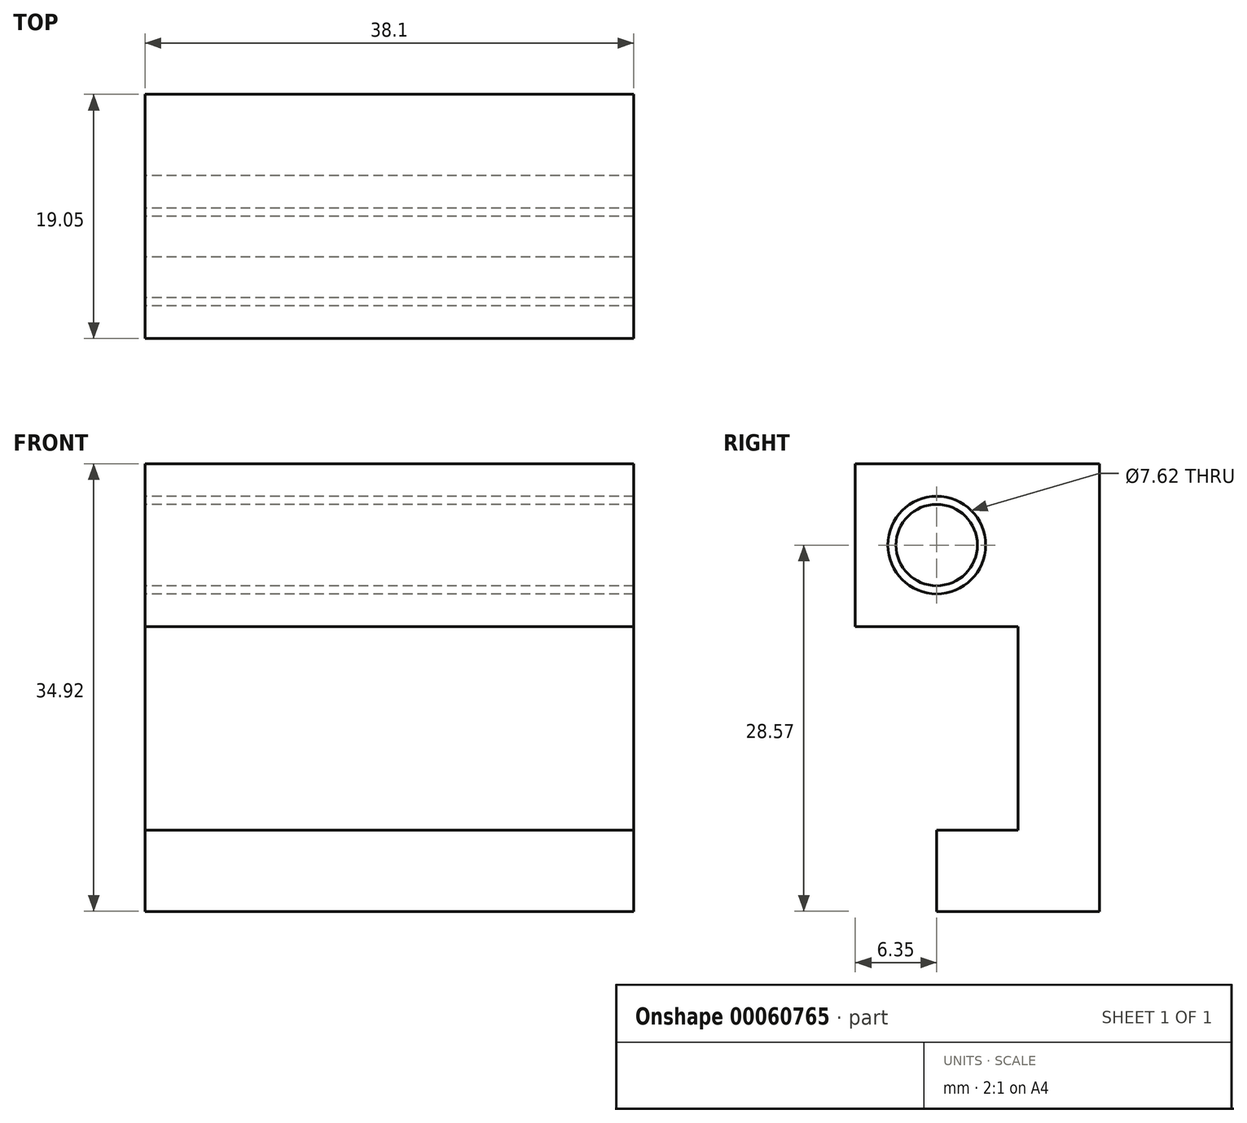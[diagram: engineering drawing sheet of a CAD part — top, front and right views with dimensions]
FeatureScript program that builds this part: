
annotation { "Feature Type Name" : "Feature", "Feature Type Description" : "" }
export const myFeature = defineFeature(function(context is Context, id is Id, definition is map)
    precondition{}
    {
        {
            var Q0;
            Q0=qCreatedBy(makeId("Right.planeOp"),FACE);
            var sketch = newSketch(context, id + "F0", { "sketchPlane" : qUnion([Q0])});
            skCircle(sketch, "E0", {"center": v(0, 0) * mm, "radius": 3.18 * mm});
            skSolve(sketch);
        }
        {
            var Q0;
            Q0 = qSketchRegion(id + "F0", true);
            extrude(context, id + "F1", {"entities" : qUnion([Q0]), "depth" : 38.1 * mm, "symmetric" : true});
        }
        {
            var Q0;
            Q0=qCreatedBy(makeId("Right.planeOp"),FACE);
            var sketch = newSketch(context, id + "F2", { "sketchPlane" : qUnion([Q0])});
            skCircle(sketch, "E1", {"center": v(0, 0) * mm, "radius": 3.81 * mm});
            skLineSegment(sketch, "E2.bottom", {"start": v(-6.35, 6.35) * mm, "end": v(12.7, 6.35) * mm});
            skLineSegment(sketch, "E2.top", {"start": v(-6.35, -6.35) * mm, "end": v(6.35, -6.35) * mm});
            skLineSegment(sketch, "E2.left", {"start": v(-6.35, 6.35) * mm, "end": v(-6.35, -6.35) * mm});
            skLineSegment(sketch, "E3.left", {"start": v(6.35, -6.35) * mm, "end": v(6.35, -22.23) * mm});
            skLineSegment(sketch, "E3.right", {"start": v(12.7, 6.35) * mm, "end": v(12.7, -28.58) * mm});
            skLineSegment(sketch, "E4.bottom", {"start": v(12.7, -28.58) * mm, "end": v(0, -28.58) * mm});
            skLineSegment(sketch, "E4.top", {"start": v(6.35, -22.23) * mm, "end": v(0, -22.23) * mm});
            skLineSegment(sketch, "E4.right", {"start": v(0, -28.58) * mm, "end": v(0, -22.23) * mm});
            skLineSegment(sketch, "E5", {"start": v(0, 0) * mm, "end": v(12.7, 0) * mm, "construction": true});
            skLineSegment(sketch, "E6", {"start": v(0, -25.4) * mm, "end": v(12.7, -25.4) * mm, "construction": true});
            skSolve(sketch);
        }
        {
            var Q0;
            Q0 = qSketchRegion(id + "F2", true);
            extrude(context, id + "F3", {"entities" : qUnion([Q0]), "depth" : 38.1 * mm, "symmetric" : true});
        }
    });
